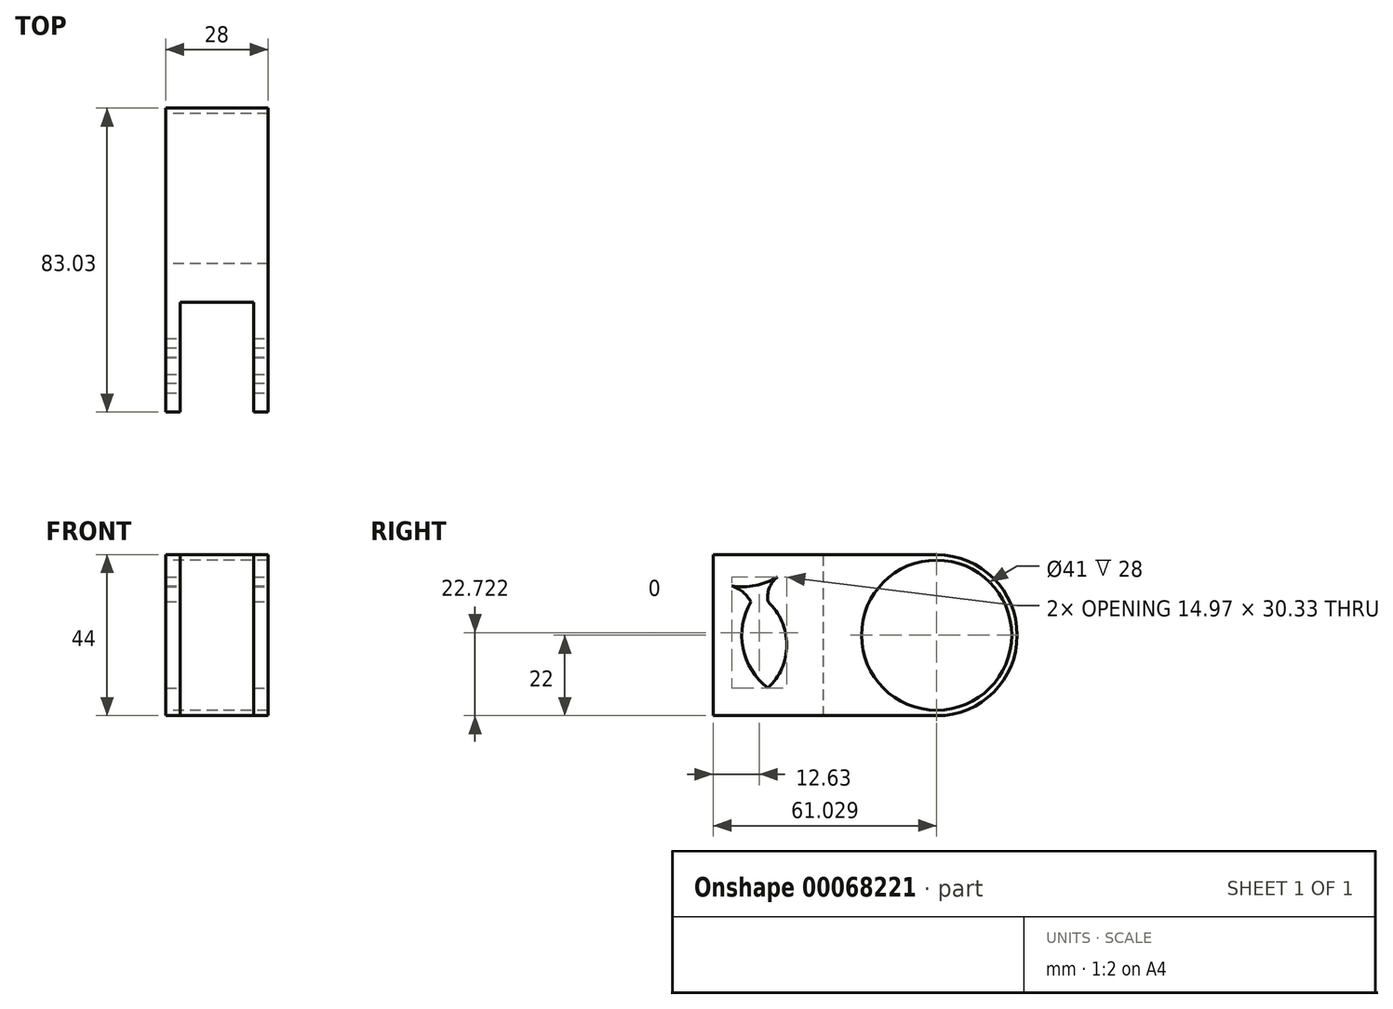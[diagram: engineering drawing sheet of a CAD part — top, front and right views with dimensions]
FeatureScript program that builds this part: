
annotation { "Feature Type Name" : "Feature", "Feature Type Description" : "" }
export const myFeature = defineFeature(function(context is Context, id is Id, definition is map)
    precondition{}
    {
        {
            var Q0;
            Q0=qCreatedBy(makeId("Top.planeOp"),FACE);
            var sketch = newSketch(context, id + "F0", { "sketchPlane" : qUnion([Q0])});
            skLineSegment(sketch, "E0.bottom", {"start": v(-10, 15) * mm, "end": v(10, 15) * mm});
            skLineSegment(sketch, "E0.left", {"start": v(-10, 15) * mm, "end": v(-10, -15) * mm});
            skLineSegment(sketch, "E0.right", {"start": v(10, 15) * mm, "end": v(10, -15) * mm});
            skPoint(sketch, "E0.middle", {"position": v(0, 0) * mm});
            skLineSegment(sketch, "E1.bottom", {"start": v(14, 25) * mm, "end": v(-14, 25) * mm});
            skLineSegment(sketch, "E2", {"start": v(-10, -15) * mm, "end": v(-14, -15) * mm});
            skLineSegment(sketch, "E3", {"start": v(10, -15) * mm, "end": v(14, -15) * mm});
            skLineSegment(sketch, "E4", {"start": v(-14, 25) * mm, "end": v(-14, -15) * mm});
            skLineSegment(sketch, "E5", {"start": v(14, 25) * mm, "end": v(14, -15) * mm});
            skSolve(sketch);
        }
        {
            var Q0;
            Q0 = qSketchRegion(id + "F0", true);
            extrude(context, id + "F1", {"entities" : qUnion([Q0]), "depth" : 22 * mm, "hasSecondDirection" : true, "secondDirectionOppositeDirection" : true, "secondDirectionDepth" : 22 * mm});
        }
        {
            var Q0;
            Q0=qCreatedBy(makeId("Right.planeOp"),FACE);
            var sketch = newSketch(context, id + "F2", { "sketchPlane" : qUnion([Q0])});
            skCircle(sketch, "E6", {"center": v(46.03, 0) * mm, "radius": 20.5 * mm});
            skCircle(sketch, "E7", {"center": v(46.03, 0) * mm, "radius": 22 * mm});
            skLineSegment(sketch, "E8", {"start": v(46.03, 22) * mm, "end": v(24.6, 22) * mm});
            skLineSegment(sketch, "E9", {"start": v(24.6, 22) * mm, "end": v(24.6, 4.96) * mm});
            skLineSegment(sketch, "E10", {"start": v(24.6, 4.96) * mm, "end": v(46.03, 22) * mm});
            skLineSegment(sketch, "E11.MirrorCS", {"start": v(46.03, -22) * mm, "end": v(24.6, -22) * mm});
            skLineSegment(sketch, "E12.MirrorCS", {"start": v(24.6, -22) * mm, "end": v(24.6, -4.96) * mm});
            skLineSegment(sketch, "E13.MirrorCS", {"start": v(24.6, -4.96) * mm, "end": v(46.03, -22) * mm});
            skArc(sketch, "E14", {"start": v(3.7, 16.62) * mm, "mid": v(-7.02, 2.15) * mm, "end": v(0, -14.44) * mm});
            skArc(sketch, "E15", {"start": v(0, -14.44) * mm, "mid": v(4.2, 2.73) * mm, "end": v(-9.85, 13.47) * mm});
            skArc(sketch, "E16", {"start": v(-9.85, 13.47) * mm, "mid": v(-2.77, 13.73) * mm, "end": v(3.7, 16.62) * mm});
            skArc(sketch, "E17", {"start": v(-4.68, 9.15) * mm, "mid": v(-6.86, 11.8) * mm, "end": v(-9.85, 13.47) * mm});
            skArc(sketch, "E18", {"start": v(3.7, 16.62) * mm, "mid": v(0.63, 13.49) * mm, "end": v(0, 9.15) * mm});
            skSolve(sketch);
        }
        {
            var Q0;
            {var subQ0=sQuery(id+"F2.wireOp",EDGE,"E10");var subQ1=sQuery(id+"F2.wireOp",EDGE,"E6");var subQ2=makeQuery(id+"F2.imprint","INTERSECT",VERTEX,{"disambiguationData":[OD(1.0)],"derivedFrom":[subQ1,subQ0]});Q0=makeQuery(id+"F2.imprint","IMPRINT",FACE,{"disambiguationData":[TD([[makeQuery(id+"F2.imprint","IMPRINT",EDGE,{"disambiguationData":[TD([[subQ2,1.0]])],"derivedFrom":subQ1}),-1.0]])]});}
            var Q1;
            {var subQ1=sQuery(id+"F2.wireOp",EDGE,"E8");Q1=makeQuery(id+"F2.imprint","IMPRINT",FACE,{"disambiguationData":[TD([[makeQuery(id+"F2.imprint","IMPRINT",EDGE,{"derivedFrom":subQ1}),1.0]])]});}
            var Q2;
            {var subQ0=sQuery(id+"F2.wireOp",EDGE,"E10");var subQ1=sQuery(id+"F2.wireOp",EDGE,"E6");var subQ2=makeQuery(id+"F2.imprint","INTERSECT",VERTEX,{"disambiguationData":[OD(0.0)],"derivedFrom":[subQ1,subQ0]});Q2=makeQuery(id+"F2.imprint","IMPRINT",FACE,{"disambiguationData":[TD([[makeQuery(id+"F2.imprint","IMPRINT",EDGE,{"disambiguationData":[TD([[subQ2,1.0]])],"derivedFrom":subQ1}),-1.0]])]});}
            var Q3;
            {var subQ0=sQuery(id+"F2.wireOp",EDGE,"E10");var subQ1=sQuery(id+"F2.wireOp",EDGE,"E6");var subQ2=makeQuery(id+"F2.imprint","INTERSECT",VERTEX,{"disambiguationData":[OD(0.0)],"derivedFrom":[subQ1,subQ0]});Q3=makeQuery(id+"F2.imprint","IMPRINT",FACE,{"disambiguationData":[TD([[makeQuery(id+"F2.imprint","IMPRINT",EDGE,{"disambiguationData":[TD([[subQ2,-1.0]])],"derivedFrom":subQ1}),-1.0]])]});}
            var Q4;
            {var subQ0=sQuery(id+"F2.wireOp",EDGE,"E13.MirrorCS");var subQ1=sQuery(id+"F2.wireOp",EDGE,"E6");var subQ2=makeQuery(id+"F2.imprint","INTERSECT",VERTEX,{"disambiguationData":[OD(0.0)],"derivedFrom":[subQ1,subQ0]});Q4=makeQuery(id+"F2.imprint","IMPRINT",FACE,{"disambiguationData":[TD([[makeQuery(id+"F2.imprint","IMPRINT",EDGE,{"disambiguationData":[TD([[subQ2,-1.0]])],"derivedFrom":subQ1}),-1.0]])]});}
            var Q5;
            {var subQ1=sQuery(id+"F2.wireOp",EDGE,"E11.MirrorCS");Q5=makeQuery(id+"F2.imprint","IMPRINT",FACE,{"disambiguationData":[TD([[makeQuery(id+"F2.imprint","IMPRINT",EDGE,{"derivedFrom":subQ1}),-1.0]])]});}
            extrude(context, id + "F3", {"entities" : qUnion([Q0, Q1, Q2, Q3, Q4, Q5]), "operationType" : NewBodyOperationType.ADD, "depth" : 14 * mm, "hasSecondDirection" : true, "secondDirectionOppositeDirection" : true, "secondDirectionDepth" : 14 * mm});
        }
        {
            var Q0;
            {var subQ0=sQuery(id+"F2.wireOp",EDGE,"E16");var subQ1=sQuery(id+"F2.wireOp",EDGE,"E14");var subQ2=makeQuery(id+"F2.imprint","INTERSECT",VERTEX,{"derivedFrom":[subQ1,subQ0]});Q0=makeQuery(id+"F2.imprint","IMPRINT",FACE,{"disambiguationData":[TD([[makeQuery(id+"F2.imprint","IMPRINT",EDGE,{"disambiguationData":[TD([[subQ2,-1.0]])],"derivedFrom":subQ1}),1.0]])]});}
            var Q1;
            {var subQ0=sQuery(id+"F2.wireOp",EDGE,"E16");var subQ1=sQuery(id+"F2.wireOp",EDGE,"E14");var subQ2=makeQuery(id+"F2.imprint","INTERSECT",VERTEX,{"derivedFrom":[subQ1,subQ0]});Q1=makeQuery(id+"F2.imprint","IMPRINT",FACE,{"disambiguationData":[TD([[makeQuery(id+"F2.imprint","IMPRINT",EDGE,{"disambiguationData":[TD([[subQ2,-1.0]])],"derivedFrom":subQ1}),-1.0]])]});}
            var Q2;
            {var subQ0=sQuery(id+"F2.wireOp",EDGE,"E17");Q2=makeQuery(id+"F2.imprint","IMPRINT",FACE,{"disambiguationData":[TD([[makeQuery(id+"F2.imprint","IMPRINT",EDGE,{"derivedFrom":subQ0}),-1.0]])]});}
            var Q3;
            {var subQ0=sQuery(id+"F2.wireOp",EDGE,"E14");var subQ1=makeQuery(id+"F2.imprint","INTERSECT",VERTEX,{"derivedFrom":[subQ0,sQuery(id+"F2.wireOp",EDGE,"E17")]});Q3=makeQuery(id+"F2.imprint","IMPRINT",FACE,{"disambiguationData":[TD([[makeQuery(id+"F2.imprint","IMPRINT",EDGE,{"disambiguationData":[TD([[subQ1,1.0]])],"derivedFrom":subQ0}),1.0]])]});}
            extrude(context, id + "F4", {"entities" : qUnion([Q0, Q1, Q2, Q3]), "operationType" : NewBodyOperationType.REMOVE, "oppositeDirection" : true, "depth" : 25 * mm, "hasSecondDirection" : true, "secondDirectionOppositeDirection" : false, "secondDirectionDepth" : 25 * mm});
        }
    });
